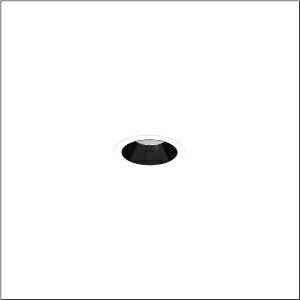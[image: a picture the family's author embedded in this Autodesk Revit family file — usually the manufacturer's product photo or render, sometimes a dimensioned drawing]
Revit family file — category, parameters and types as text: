
# Revit family: lunis_21_s_51db17ta91c
name_source: partatom
category: Lighting Fixtures
units: mm (PartAtom-declared; Revit-internal decimal feet)

## family parameters
Cut with Voids When Loaded = No
Host = Face
Light Source = No
Part Type = Normal
Room Calculation Point = No
Round Connector Dimension = Use Diameter
Shared = No

## types (1)
- --- (1 x LED 3000 K ... 6500 K, 1070 lm, 8 W, 4000K)
    Apparent Load = 8 VA
    CIE Flux Codes = 97 100 100 100 100
    Color Rendering = 80
    Color Temperature = 4000K
    Default Elevation = 1800 mm
    Description = Lunis 21,  S, downlight, light control with lens, of PMMA, anti glare with reflector, of plastic, light emission: direct distribution, LED rated luminous flux: 1.070lm, light colour: 8tw, with terminal, 5-pole, mains connection: 220..240V, AC, 50..60Hz, housing, round, of diecast aluminium, traffic white (RAL 9016), diameter: 84mm, clamping range: 1..40mm, protection rating (complete): IP20, protection rating (on room side): IP54, insulation class (complete): insulation class II (safety insulation), certification: CE, impact resistance: IK03, packaging unit: 1 piece
    Height = 0 mm  [stored 0 ft]
    Lamp = 1 x LED 3000 K ... 6500 K
    Lamp Light Flux = 1070 lm
    Lamp Power = 8 W
    Lamp count = 1
    Length = 84 mm
    Luminous efficacy = 134 lm/W
    Manufacturer = Siteco
    ModVariant = No
    Model = 51DB17TA91C
    Mounting Place = Ceiling
    Mounting Type = Recessed
    Number of Poles = 1
    OnlyDefault = Yes
    Power Factor = 1
    Product Name = Lunis 21 S
    Product group = downlight
    ProductGroupID = 400
    Protection Class = Protection class II
    Protection Degree = IP 20
    RLX_Detail_Level = 1
    RLX_Emergency_Light_Flux = 0 lm
    RLX_Emergency_Type = 0
    RLX_Emergency_Type_DB = No
    RlxData = <blob elided: 8857 chars, md5=bf1c3cda>
    Socket = socket
    Standby Power = 0 W
    System Light Flux = 1070 lm
    System Power = 8 W
    Type Comments = individual setting: CCT=4000K, colour temperature 4000K, luminous flux: 100 % | (OFF | OFF | ON | OFF) | 200 mA
    Type Image = l_1290844.jpg
    URL = http://relux.com
    VarID = @adj_020210
    Voltage = 0 V
    Weight = 0.00 kg
    Width = 0 mm  [stored 0 ft]

note: [stored X ft] marks values corroborated as IEEE doubles in the binary element streams (Revit-internal decimal feet)

## geometry (parser evidence)
native form markers: Sweep x8
no freeform markers — native parametric forms only
